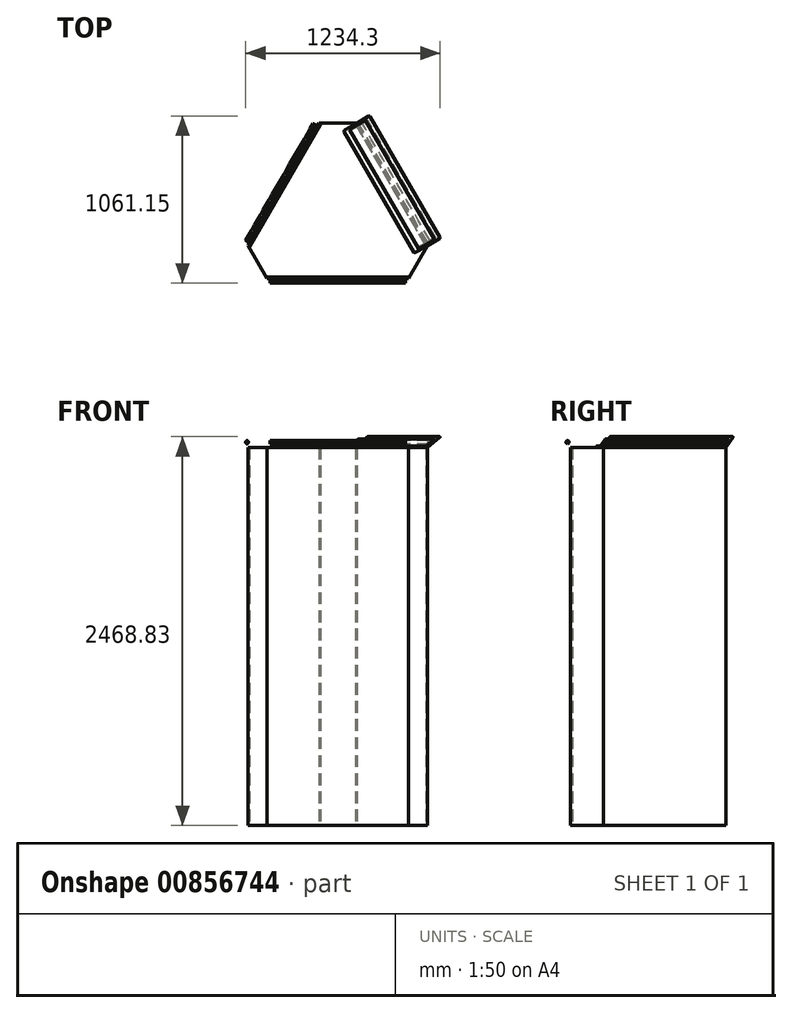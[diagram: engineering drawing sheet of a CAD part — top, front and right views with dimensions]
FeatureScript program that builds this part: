
annotation { "Feature Type Name" : "Feature", "Feature Type Description" : "" }
export const myFeature = defineFeature(function(context is Context, id is Id, definition is map)
    precondition{}
    {
        {
            var Q0;
            Q0=qCreatedBy(makeId("Top.planeOp"),FACE);
            var sketch = newSketch(context, id + "F0", { "sketchPlane" : qUnion([Q0])});
            skLineSegment(sketch, "E0", {"start": v(-570, 207.85) * mm, "end": v(-120, 987.27) * mm});
            skLineSegment(sketch, "E1", {"start": v(120, 987.27) * mm, "end": v(570, 207.85) * mm});
            skLineSegment(sketch, "E2", {"start": v(-450, 0) * mm, "end": v(450, 0) * mm});
            skLineSegment(sketch, "E3", {"start": v(-690, 0) * mm, "end": v(345, 597.56) * mm, "construction": true});
            skLineSegment(sketch, "E4", {"start": v(690, 0) * mm, "end": v(-345, 597.56) * mm, "construction": true});
            skLineSegment(sketch, "E5", {"start": v(0, 1195.12) * mm, "end": v(0, 0) * mm, "construction": true});
            skLineSegment(sketch, "E6", {"start": v(-120, 987.27) * mm, "end": v(120, 987.27) * mm});
            skLineSegment(sketch, "E7", {"start": v(-450, 0) * mm, "end": v(-570, 207.85) * mm});
            skLineSegment(sketch, "E8", {"start": v(450, 0) * mm, "end": v(570, 207.85) * mm});
            skSolve(sketch);
        }
        {
            var Q0;
            Q0=qSketchRegion(id+"F0",true);
            extrude(context, id + "F1", {"entities" : qUnion([Q0]), "depth" : 2400 * mm, "offsetDistance" : 25 * mm});
        }
        {
            var Q0;
            Q0=makeQuery(id+"F1.opExtrude","CAP_FACE",FACE,{"disambiguationData":[OSD([sQuery(id+"F0.wireOp",EDGE,"E0"),sQuery(id+"F0.wireOp",EDGE,"E1"),sQuery(id+"F0.wireOp",EDGE,"E2"),sQuery(id+"F0.wireOp",EDGE,"E6"),sQuery(id+"F0.wireOp",EDGE,"E7"),sQuery(id+"F0.wireOp",EDGE,"E8")])],"isStart":false});
            var sketch = newSketch(context, id + "F2", { "sketchPlane" : qUnion([Q0])});
            skLineSegment(sketch, "E9.0", {"start": v(-350, 40) * mm, "end": v(350, 40) * mm});
            skLineSegment(sketch, "E10.0", {"start": v(-485.36, 274.45) * mm, "end": v(-135.36, 880.67) * mm});
            skLineSegment(sketch, "E11", {"start": v(-350, 40) * mm, "end": v(-350, 90) * mm});
            skLineSegment(sketch, "E12", {"start": v(-350, 90) * mm, "end": v(350, 90) * mm});
            skLineSegment(sketch, "E13", {"start": v(350, 90) * mm, "end": v(350, 40) * mm});
            skLineSegment(sketch, "E14", {"start": v(-135.36, 880.67) * mm, "end": v(-92.06, 855.67) * mm});
            skLineSegment(sketch, "E15", {"start": v(-92.06, 855.67) * mm, "end": v(-442.06, 249.45) * mm});
            skLineSegment(sketch, "E16", {"start": v(-442.06, 249.45) * mm, "end": v(-485.36, 274.45) * mm});
            skLineSegment(sketch, "E17", {"start": v(-345, 597.56) * mm, "end": v(-140.02, 479.21) * mm, "construction": true});
            skLineSegment(sketch, "E18", {"start": v(0, 0) * mm, "end": v(0, 987.27) * mm, "construction": true});
            skLineSegment(sketch, "E19.MirrorCS", {"start": v(-92.06, 855.67) * mm, "end": v(-135.36, 880.67) * mm});
            skLineSegment(sketch, "E20.MirrorCS", {"start": v(-485.36, 274.45) * mm, "end": v(-442.06, 249.45) * mm});
            skLineSegment(sketch, "E21.MirrorCS", {"start": v(-135.36, 880.67) * mm, "end": v(-485.36, 274.45) * mm});
            skLineSegment(sketch, "E22.MirrorCS", {"start": v(-442.06, 249.45) * mm, "end": v(-92.06, 855.67) * mm});
            skLineSegment(sketch, "E23.MirrorCS", {"start": v(135.36, 880.67) * mm, "end": v(92.06, 855.67) * mm});
            skLineSegment(sketch, "E24.MirrorCS", {"start": v(442.06, 249.45) * mm, "end": v(485.36, 274.45) * mm});
            skLineSegment(sketch, "E25.MirrorCS", {"start": v(485.36, 274.45) * mm, "end": v(442.06, 249.45) * mm});
            skLineSegment(sketch, "E26.MirrorCS", {"start": v(92.06, 855.67) * mm, "end": v(135.36, 880.67) * mm});
            skLineSegment(sketch, "E27.MirrorCS", {"start": v(92.06, 855.67) * mm, "end": v(442.06, 249.45) * mm});
            skLineSegment(sketch, "E28.MirrorCS", {"start": v(485.36, 274.45) * mm, "end": v(135.36, 880.67) * mm});
            skLineSegment(sketch, "E29.MirrorCS", {"start": v(135.36, 880.67) * mm, "end": v(485.36, 274.45) * mm});
            skLineSegment(sketch, "E30.MirrorCS", {"start": v(442.06, 249.45) * mm, "end": v(92.06, 855.67) * mm});
            skSolve(sketch);
        }
        {
            var Q0;
            Q0=qCreatedBy(makeId("Right.planeOp"),FACE);
            var sketch = newSketch(context, id + "F3", { "sketchPlane" : qUnion([Q0])});
            skPoint(sketch, "E31.2", {"position": v(103.92, 2400) * mm});
            skLineSegment(sketch, "E32", {"start": v(398.37, 2400) * mm, "end": v(398.37, -119.7) * mm, "construction": true});
            skPoint(sketch, "E32.endSnap0", {"position": v(398.37, 2400) * mm});
            skSolve(sketch);
        }
        {
            var Q0;
            Q0=makeQuery(id+"F1.opExtrude","CAP_FACE",FACE,{"disambiguationData":[OSD([sQuery(id+"F0.wireOp",EDGE,"E0"),sQuery(id+"F0.wireOp",EDGE,"E1"),sQuery(id+"F0.wireOp",EDGE,"E2"),sQuery(id+"F0.wireOp",EDGE,"E6"),sQuery(id+"F0.wireOp",EDGE,"E7"),sQuery(id+"F0.wireOp",EDGE,"E8")])],"isStart":true});
            var sketch = newSketch(context, id + "F4", { "sketchPlane" : qUnion([Q0])});
            skLineSegment(sketch, "E33.0", {"start": v(-570, -207.85) * mm, "end": v(-120, -987.27) * mm});
            skLineSegment(sketch, "E33.1", {"start": v(120, -987.27) * mm, "end": v(570, -207.85) * mm});
            skLineSegment(sketch, "E33.2", {"start": v(-450, 0) * mm, "end": v(450, 0) * mm});
            skLineSegment(sketch, "E34.0", {"start": v(-561.34, -202.85) * mm, "end": v(-111.34, -982.27) * mm});
            skLineSegment(sketch, "E35.0", {"start": v(-450, -10) * mm, "end": v(450, -10) * mm});
            skLineSegment(sketch, "E36.0", {"start": v(111.34, -982.27) * mm, "end": v(561.34, -202.85) * mm});
            skLineSegment(sketch, "E37", {"start": v(-111.34, -982.27) * mm, "end": v(-120, -987.27) * mm});
            skLineSegment(sketch, "E38", {"start": v(-570, -207.85) * mm, "end": v(-561.34, -202.85) * mm});
            skLineSegment(sketch, "E39", {"start": v(-450, 0) * mm, "end": v(-450, -10) * mm});
            skLineSegment(sketch, "E40", {"start": v(450, 0) * mm, "end": v(450, -10) * mm});
            skLineSegment(sketch, "E41", {"start": v(570, -207.85) * mm, "end": v(561.34, -202.85) * mm});
            skLineSegment(sketch, "E42", {"start": v(120, -987.27) * mm, "end": v(111.34, -982.27) * mm});
            skSolve(sketch);
        }
        {
            var Q0;
            Q0=qSketchRegion(id+"F4",true);
            var Q1;
            Q1=makeQuery(id+"F1.opExtrude","CAP_FACE",FACE,{"disambiguationData":[OSD([sQuery(id+"F0.wireOp",EDGE,"E0"),sQuery(id+"F0.wireOp",EDGE,"E1"),sQuery(id+"F0.wireOp",EDGE,"E2"),sQuery(id+"F0.wireOp",EDGE,"E6"),sQuery(id+"F0.wireOp",EDGE,"E7"),sQuery(id+"F0.wireOp",EDGE,"E8")])],"isStart":false});
            extrude(context, id + "F5", {"entities" : qUnion([Q0]), "operationType" : NewBodyOperationType.REMOVE, "endBound" : BoundingType.UP_TO_SURFACE, "oppositeDirection" : true, "depth" : 25 * mm, "endBoundEntityFace" : qUnion([Q1]), "offsetDistance" : 25 * mm});
        }
        {
            var Q0;
            Q0=makeQuery(id+"F1.opExtrude","CAP_FACE",FACE,{"disambiguationData":[OSD([sQuery(id+"F0.wireOp",EDGE,"E0"),sQuery(id+"F0.wireOp",EDGE,"E1"),sQuery(id+"F0.wireOp",EDGE,"E2"),sQuery(id+"F0.wireOp",EDGE,"E6"),sQuery(id+"F0.wireOp",EDGE,"E7"),sQuery(id+"F0.wireOp",EDGE,"E8")])],"isStart":true});
            var sketch = newSketch(context, id + "F6", { "sketchPlane" : qUnion([Q0])});
            skLineSegment(sketch, "E43.0", {"start": v(-560.84, -203.71) * mm, "end": v(-111.84, -981.4) * mm});
            skLineSegment(sketch, "E44.0", {"start": v(-569.5, -208.71) * mm, "end": v(-120.5, -986.4) * mm});
            skLineSegment(sketch, "E45.0", {"start": v(-111.84, -981.4) * mm, "end": v(-120.5, -986.4) * mm});
            skLineSegment(sketch, "E46.0", {"start": v(-569.5, -208.71) * mm, "end": v(-560.84, -203.71) * mm});
            skPoint(sketch, "E47.orphan", {"position": v(-561.34, -202.85) * mm});
            skPoint(sketch, "E48.orphan", {"position": v(-111.34, -982.27) * mm});
            skSolve(sketch);
        }
        {
            var Q0;
            Q0=qSketchRegion(id+"F6",true);
            var Q1;
            Q1=makeQuery(id+"F1.opExtrude","CAP_FACE",FACE,{"disambiguationData":[OSD([sQuery(id+"F0.wireOp",EDGE,"E0"),sQuery(id+"F0.wireOp",EDGE,"E1"),sQuery(id+"F0.wireOp",EDGE,"E2"),sQuery(id+"F0.wireOp",EDGE,"E6"),sQuery(id+"F0.wireOp",EDGE,"E7"),sQuery(id+"F0.wireOp",EDGE,"E8")])],"isStart":false});
            extrude(context, id + "F7", {"entities" : qUnion([Q0]), "endBound" : BoundingType.UP_TO_SURFACE, "oppositeDirection" : true, "depth" : 25 * mm, "endBoundEntityFace" : qUnion([Q1]), "offsetDistance" : 25 * mm});
        }
        {
            var Q0;
            Q0=makeQuery(id+"F7.opExtrude","SWEPT_BODY",BODY,{"disambiguationData":[OSD([sQuery(id+"F6.wireOp",EDGE,"E43.0"),sQuery(id+"F6.wireOp",EDGE,"E44.0"),sQuery(id+"F6.wireOp",EDGE,"E45.0"),sQuery(id+"F6.wireOp",EDGE,"E46.0")])]});
            var Q1;
            Q1=sQuery(id+"F3.wireOp",EDGE,"E32");
            circularPattern(context, id + "F8", {"entities" : qUnion([Q0]), "axis" : qUnion([Q1]), "angle" : 360 * degree, "instanceCount" : 3, "equalSpace" : true});
        }
        {
            var Q0;
            Q0=makeQuery(id+"F1.opExtrude","SWEPT_FACE",FACE,{"disambiguationData":[OSD([sQuery(id+"F0.wireOp",EDGE,"E7")])]});
            var Q1;
            Q1=makeQuery(id+"F7.opExtrude","SWEPT_EDGE",EDGE,{"disambiguationData":[OSD([sQuery(id+"F6.wireOp",EDGE,"E44.0"),sQuery(id+"F6.wireOp",EDGE,"E46.0")])]});
            cPlane(context, id + "F9", {"entities" : qUnion([Q0, Q1]), "cplaneType" : CPlaneType.LINE_ANGLE, "offset" : 25 * mm, "angle" : 90 * degree, "width" : 150 * mm, "height" : 150 * mm});
        }
        {
            var Q0;
            Q0=qCreatedBy(id+"F9.planeOp",FACE);
            cPlane(context, id + "F10", {"entities" : qUnion([Q0]), "cplaneType" : CPlaneType.OFFSET, "offset" : 120.5 * mm, "width" : 150 * mm, "height" : 150 * mm});
        }
        {
            var Q0;
            Q0=qCreatedBy(id+"F10.planeOp",FACE);
            var sketch = newSketch(context, id + "F11", { "sketchPlane" : qUnion([Q0])});
            skPoint(sketch, "E49.0", {"position": v(597.56, 2400) * mm});
            skLineSegment(sketch, "E50", {"start": v(597.56, 2400) * mm, "end": v(695.86, 2468.83) * mm});
            skLineSegment(sketch, "E51", {"start": v(695.86, 2468.83) * mm, "end": v(675.86, 2468.83) * mm});
            skLineSegment(sketch, "E52", {"start": v(675.86, 2468.83) * mm, "end": v(591.84, 2410) * mm});
            skLineSegment(sketch, "E53", {"start": v(577.56, 2400) * mm, "end": v(597.56, 2400) * mm});
            skLineSegment(sketch, "E54", {"start": v(577.56, 2400) * mm, "end": v(527.56, 2400) * mm});
            skLineSegment(sketch, "E55", {"start": v(527.56, 2400) * mm, "end": v(527.56, 2410) * mm});
            skLineSegment(sketch, "E56", {"start": v(527.56, 2410) * mm, "end": v(591.84, 2410) * mm});
            skSolve(sketch);
        }
        {
            var Q0;
            Q0 = qSketchRegion(id + "F11", true);
            var Q1;
            Q1=makeQuery(id+"F8.opPattern","COPY",EDGE,{"derivedFrom":makeQuery(id+"F7.opExtrude","CAP_EDGE",EDGE,{"disambiguationData":[OSD([sQuery(id+"F6.wireOp",EDGE,"E44.0")])],"isStart":false}),"instanceName":"1"});
            sweep(context, id + "F12", {"profiles" : qUnion([Q0]), "path" : qUnion([Q1])});
        }
        {
            var Q0;
            Q0=makeQuery(id+"F12.opSweep","SWEPT_FACE",FACE,{"disambiguationData":[OSD([sQuery(id+"F0.wireOp",EDGE,"E0"),sQuery(id+"F0.wireOp",EDGE,"E1"),sQuery(id+"F0.wireOp",EDGE,"E2"),sQuery(id+"F0.wireOp",EDGE,"E6"),sQuery(id+"F0.wireOp",EDGE,"E7"),sQuery(id+"F0.wireOp",EDGE,"E8"),sQuery(id+"F6.wireOp",EDGE,"E44.0"),sQuery(id+"F11.wireOp",EDGE,"E55")])]});
            var sketch = newSketch(context, id + "F13", { "sketchPlane" : qUnion([Q0])});
            skLineSegment(sketch, "E57.bottom", {"start": v(-774, 2410) * mm, "end": v(84, 2410) * mm});
            skLineSegment(sketch, "E57.top", {"start": v(-774, 2448.83) * mm, "end": v(84, 2448.83) * mm});
            skLineSegment(sketch, "E57.left", {"start": v(-774, 2410) * mm, "end": v(-774, 2448.83) * mm});
            skLineSegment(sketch, "E57.right", {"start": v(84, 2410) * mm, "end": v(84, 2448.83) * mm});
            skSolve(sketch);
        }
        {
            var Q0;
            Q0 = qSketchRegion(id + "F13", true);
            extrude(context, id + "F14", {"entities" : qUnion([Q0]), "operationType" : NewBodyOperationType.REMOVE, "oppositeDirection" : true, "depth" : 301 * mm, "offsetDistance" : 25 * mm});
        }
        {
            var Q0;
            Q0=makeQuery(id+"F12.opSweep","CAP_FACE",FACE,{"disambiguationData":[OSD([sQuery(id+"F0.wireOp",EDGE,"E0"),sQuery(id+"F0.wireOp",EDGE,"E1"),sQuery(id+"F0.wireOp",EDGE,"E2"),sQuery(id+"F0.wireOp",EDGE,"E6"),sQuery(id+"F0.wireOp",EDGE,"E7"),sQuery(id+"F0.wireOp",EDGE,"E8"),sQuery(id+"F6.wireOp",EDGE,"E44.0"),sQuery(id+"F6.wireOp",EDGE,"E46.0"),sQuery(id+"F11.wireOp",EDGE,"E50"),sQuery(id+"F11.wireOp",EDGE,"E51"),sQuery(id+"F11.wireOp",EDGE,"E52"),sQuery(id+"F11.wireOp",EDGE,"E53"),sQuery(id+"F11.wireOp",EDGE,"E54"),sQuery(id+"F11.wireOp",EDGE,"E55"),sQuery(id+"F11.wireOp",EDGE,"E56")])],"isStart":true});
            var sketch = newSketch(context, id + "F15", { "sketchPlane" : qUnion([Q0])});
            skLineSegment(sketch, "E58.0", {"start": v(-546.84, 2410) * mm, "end": v(-538.12, 2410) * mm});
            skLineSegment(sketch, "E58.1", {"start": v(-654.43, 2453.83) * mm, "end": v(-647.3, 2448.83) * mm});
            skPoint(sketch, "E59.0", {"position": v(-657.3, 2448.83) * mm});
            skLineSegment(sketch, "E60", {"start": v(-647.3, 2448.83) * mm, "end": v(-602.3, 2448.83) * mm});
            skLineSegment(sketch, "E61", {"start": v(-602.3, 2448.83) * mm, "end": v(-546.84, 2410) * mm});
            skLineSegment(sketch, "E62.0", {"start": v(-600.72, 2453.83) * mm, "end": v(-538.12, 2410) * mm});
            skLineSegment(sketch, "E62.1", {"start": v(-654.43, 2453.83) * mm, "end": v(-600.72, 2453.83) * mm});
            skPoint(sketch, "E63.orphan", {"position": v(-675.86, 2468.83) * mm});
            skPoint(sketch, "E64.orphan", {"position": v(-591.84, 2410) * mm});
            skPoint(sketch, "E65.orphan", {"position": v(-527.56, 2410) * mm});
            skSolve(sketch);
        }
        {
            var Q0;
            Q0 = qSketchRegion(id + "F15", true);
            var Q1;
            Q1=makeQuery(id+"F14.boolean.opBoolean","COPY",FACE,{"derivedFrom":makeQuery(id+"F14.opExtrude","SWEPT_FACE",FACE,{"disambiguationData":[OSD([sQuery(id+"F13.wireOp",EDGE,"E57.right")])]})});
            extrude(context, id + "F16", {"entities" : qUnion([Q0]), "operationType" : NewBodyOperationType.ADD, "endBound" : BoundingType.UP_TO_SURFACE, "oppositeDirection" : true, "depth" : 25 * mm, "endBoundEntityFace" : qUnion([Q1]), "hasOffset" : true, "offsetDistance" : 10 * mm, "offsetOppositeDirection" : true});
        }
        {
            var Q0;
            Q0=makeQuery(id+"F16.opExtrude","CAP_FACE",FACE,{"disambiguationData":[OSD([sQuery(id+"F15.wireOp",EDGE,"E58.0"),sQuery(id+"F15.wireOp",EDGE,"E58.1"),sQuery(id+"F15.wireOp",EDGE,"E60"),sQuery(id+"F15.wireOp",EDGE,"E61"),sQuery(id+"F15.wireOp",EDGE,"E62.0"),sQuery(id+"F15.wireOp",EDGE,"E62.1")])],"isStart":false});
            var sketch = newSketch(context, id + "F17", { "sketchPlane" : qUnion([Q0])});
            skLineSegment(sketch, "E66.0", {"start": v(600.72, 2453.83) * mm, "end": v(538.12, 2410) * mm});
            skLineSegment(sketch, "E66.1", {"start": v(654.43, 2453.83) * mm, "end": v(600.72, 2453.83) * mm});
            skPoint(sketch, "E66.2", {"position": v(569.42, 2431.91) * mm});
            skLineSegment(sketch, "E67.0", {"start": v(654.43, 2453.83) * mm, "end": v(591.84, 2410) * mm});
            skLineSegment(sketch, "E67.1", {"start": v(591.84, 2410) * mm, "end": v(538.12, 2410) * mm});
            skPoint(sketch, "E68.orphan", {"position": v(527.56, 2410) * mm});
            skPoint(sketch, "E69.orphan", {"position": v(675.86, 2468.83) * mm});
            skSolve(sketch);
        }
        {
            var Q0;
            Q0 = qSketchRegion(id + "F17", true);
            var Q1;
            Q1 = qConstructionFilter(qBodyType(qCreatedBy(id + "F17" ,EDGE), BodyType.WIRE), ConstructionObject.NO);
            extrude(context, id + "F18", {"entities" : qUnion([Q0]), "operationType" : NewBodyOperationType.ADD, "surfaceOperationType" : NewSurfaceOperationType.ADD, "surfaceEntities" : qUnion([Q1]), "oppositeDirection" : true, "depth" : 10 * mm, "offsetDistance" : 25 * mm});
        }
        {
            var Q0;
            Q0=makeQuery(id+"F12.opSweep","SWEPT_FACE",FACE,{"disambiguationData":[OSD([sQuery(id+"F0.wireOp",EDGE,"E0"),sQuery(id+"F0.wireOp",EDGE,"E1"),sQuery(id+"F0.wireOp",EDGE,"E2"),sQuery(id+"F0.wireOp",EDGE,"E6"),sQuery(id+"F0.wireOp",EDGE,"E7"),sQuery(id+"F0.wireOp",EDGE,"E8"),sQuery(id+"F6.wireOp",EDGE,"E44.0"),sQuery(id+"F11.wireOp",EDGE,"E55")])]});
            var sketch = newSketch(context, id + "F19", { "sketchPlane" : qUnion([Q0])});
            skLineSegment(sketch, "E70.bottom", {"start": v(-794, 2410) * mm, "end": v(-784, 2410) * mm});
            skLineSegment(sketch, "E70.top", {"start": v(-794, 2453.83) * mm, "end": v(-784, 2453.83) * mm});
            skLineSegment(sketch, "E70.left", {"start": v(-794, 2410) * mm, "end": v(-794, 2453.83) * mm});
            skLineSegment(sketch, "E70.right", {"start": v(-784, 2410) * mm, "end": v(-784, 2453.83) * mm});
            skSolve(sketch);
        }
        {
            var Q0;
            Q0 = qSketchRegion(id + "F19", true);
            var Q1;
            {var subQ1=sQuery(id+"F6.wireOp",EDGE,"E44.0");var subQ2=sQuery(id+"F11.wireOp",EDGE,"E52");Q1=makeQuery(id+"F16.boolean.opBoolean","SPLIT",FACE,{"disambiguationData":[TD([makeQuery(id+"F14.boolean.opBoolean","COPY",FACE,{"derivedFrom":makeQuery(id+"F14.opExtrude","SWEPT_FACE",FACE,{"disambiguationData":[OSD([sQuery(id+"F13.wireOp",EDGE,"E57.left")])]})})])],"derivedFrom":makeQuery(id+"F12.opSweep","SWEPT_FACE",FACE,{"disambiguationData":[OSD([subQ1,subQ2])]})});}
            extrude(context, id + "F20", {"entities" : qUnion([Q0]), "operationType" : NewBodyOperationType.REMOVE, "endBound" : BoundingType.UP_TO_SURFACE, "oppositeDirection" : true, "depth" : 25 * mm, "endBoundEntityFace" : qUnion([Q1]), "offsetDistance" : 25 * mm});
        }
        {
            var Q0;
            Q0=makeQuery(id+"F20.boolean.opBoolean","COPY",FACE,{"derivedFrom":makeQuery(id+"F20.opExtrude","SWEPT_FACE",FACE,{"disambiguationData":[OSD([sQuery(id+"F19.wireOp",EDGE,"E70.right")])]})});
            var sketch = newSketch(context, id + "F21", { "sketchPlane" : qUnion([Q0])});
            skLineSegment(sketch, "E71.0", {"start": v(-654.43, 2453.83) * mm, "end": v(-600.72, 2453.83) * mm});
            skLineSegment(sketch, "E71.1", {"start": v(-600.72, 2453.83) * mm, "end": v(-538.12, 2410) * mm});
            skLineSegment(sketch, "E72.0", {"start": v(-654.43, 2453.83) * mm, "end": v(-591.84, 2410) * mm});
            skLineSegment(sketch, "E72.1", {"start": v(-591.84, 2410) * mm, "end": v(-538.12, 2410) * mm});
            skPoint(sketch, "E73.orphan", {"position": v(-675.86, 2468.83) * mm});
            skPoint(sketch, "E74.orphan", {"position": v(-527.56, 2410) * mm});
            skSolve(sketch);
        }
        {
            var Q0;
            Q0 = qSketchRegion(id + "F21", true);
            extrude(context, id + "F22", {"entities" : qUnion([Q0]), "operationType" : NewBodyOperationType.ADD, "oppositeDirection" : true, "depth" : 10 * mm, "offsetDistance" : 25 * mm});
        }
        {
            var Q0;
            Q0=makeQuery(id+"F12.opSweep","SWEPT_FACE",FACE,{"disambiguationData":[OSD([sQuery(id+"F0.wireOp",EDGE,"E0"),sQuery(id+"F0.wireOp",EDGE,"E1"),sQuery(id+"F0.wireOp",EDGE,"E2"),sQuery(id+"F0.wireOp",EDGE,"E6"),sQuery(id+"F0.wireOp",EDGE,"E7"),sQuery(id+"F0.wireOp",EDGE,"E8"),sQuery(id+"F6.wireOp",EDGE,"E44.0"),sQuery(id+"F11.wireOp",EDGE,"E55")])]});
            extrude(context, id + "F23", {"entities" : qUnion([Q0]), "operationType" : NewBodyOperationType.ADD, "depth" : 25 * mm, "offsetDistance" : 25 * mm});
        }
        {
            var Q0;
            Q0=makeQuery(id+"F18.boolean.opBoolean","MERGE",FACE,{"derivedFrom":[makeQuery(id+"F14.boolean.opBoolean","COPY",FACE,{"derivedFrom":makeQuery(id+"F14.opExtrude","SWEPT_FACE",FACE,{"disambiguationData":[OSD([sQuery(id+"F13.wireOp",EDGE,"E57.right")])]})}),makeQuery(id+"F18.opExtrude","CAP_FACE",FACE,{"disambiguationData":[OSD([sQuery(id+"F17.wireOp",EDGE,"E66.0"),sQuery(id+"F17.wireOp",EDGE,"E66.1"),sQuery(id+"F17.wireOp",EDGE,"E67.0"),sQuery(id+"F17.wireOp",EDGE,"E67.1")])],"isStart":false})]});
            var sketch = newSketch(context, id + "F24", { "sketchPlane" : qUnion([Q0])});
            skLineSegment(sketch, "E75.0", {"start": v(-611.84, 2410) * mm, "end": v(-546.84, 2410) * mm});
            skLineSegment(sketch, "E75.1", {"start": v(-597.56, 2400) * mm, "end": v(-611.84, 2410) * mm});
            skLineSegment(sketch, "E76.0", {"start": v(-532.56, 2400) * mm, "end": v(-597.56, 2400) * mm});
            skLineSegment(sketch, "E77", {"start": v(-546.84, 2410) * mm, "end": v(-532.56, 2400) * mm});
            skPoint(sketch, "E78.orphan", {"position": v(-695.86, 2468.83) * mm});
            skPoint(sketch, "E79.orphan", {"position": v(-502.56, 2400) * mm});
            skSolve(sketch);
        }
        {
            var Q0;
            Q0 = qSketchRegion(id + "F24", true);
            var Q1;
            Q1=makeQuery(id+"F22.boolean.opBoolean","MERGE",FACE,{"derivedFrom":[makeQuery(id+"F14.boolean.opBoolean","COPY",FACE,{"derivedFrom":makeQuery(id+"F14.opExtrude","SWEPT_FACE",FACE,{"disambiguationData":[OSD([sQuery(id+"F13.wireOp",EDGE,"E57.left")])]})}),makeQuery(id+"F22.opExtrude","CAP_FACE",FACE,{"disambiguationData":[OSD([sQuery(id+"F21.wireOp",EDGE,"E71.0"),sQuery(id+"F21.wireOp",EDGE,"E71.1"),sQuery(id+"F21.wireOp",EDGE,"E72.0"),sQuery(id+"F21.wireOp",EDGE,"E72.1")])],"isStart":false})]});
            extrude(context, id + "F25", {"entities" : qUnion([Q0]), "operationType" : NewBodyOperationType.REMOVE, "endBound" : BoundingType.UP_TO_SURFACE, "depth" : 25 * mm, "endBoundEntityFace" : qUnion([Q1]), "offsetDistance" : 25 * mm});
        }
        {
            var Q0;
            Q0=makeQuery(id+"F25.boolean.opBoolean","MERGE",FACE,{"derivedFrom":[makeQuery(id+"F22.boolean.opBoolean","MERGE",FACE,{"derivedFrom":[makeQuery(id+"F14.boolean.opBoolean","COPY",FACE,{"derivedFrom":makeQuery(id+"F14.opExtrude","SWEPT_FACE",FACE,{"disambiguationData":[OSD([sQuery(id+"F13.wireOp",EDGE,"E57.left")])]})}),makeQuery(id+"F22.opExtrude","CAP_FACE",FACE,{"disambiguationData":[OSD([sQuery(id+"F21.wireOp",EDGE,"E71.0"),sQuery(id+"F21.wireOp",EDGE,"E71.1"),sQuery(id+"F21.wireOp",EDGE,"E72.0"),sQuery(id+"F21.wireOp",EDGE,"E72.1")])],"isStart":false})]})],"fromTools":[makeQuery(id+"F25.opExtrude","CAP_FACE",FACE,{"disambiguationData":[OSD([sQuery(id+"F24.wireOp",EDGE,"E75.0"),sQuery(id+"F24.wireOp",EDGE,"E75.1"),sQuery(id+"F24.wireOp",EDGE,"E76.0"),sQuery(id+"F24.wireOp",EDGE,"E77")])],"isStart":false})]});
            var sketch = newSketch(context, id + "F26", { "sketchPlane" : qUnion([Q0])});
            skLineSegment(sketch, "E80.0", {"start": v(667.3, 2448.83) * mm, "end": v(602.3, 2448.83) * mm, "construction": true});
            skLineSegment(sketch, "E80.1", {"start": v(532.56, 2400) * mm, "end": v(602.3, 2448.83) * mm, "construction": true});
            skLineSegment(sketch, "E80.2", {"start": v(667.3, 2448.83) * mm, "end": v(597.56, 2400) * mm, "construction": true});
            skPoint(sketch, "E80.3", {"position": v(632.43, 2424.41) * mm});
            skCircle(sketch, "E81", {"center": v(617.43, 2433.83) * mm, "radius": 10 * mm});
            skSolve(sketch);
        }
        {
            var Q0;
            Q0 = qSketchRegion(id + "F26", true);
            var Q1;
            Q1=makeQuery(id+"F25.boolean.opBoolean","MERGE",FACE,{"derivedFrom":[makeQuery(id+"F18.boolean.opBoolean","MERGE",FACE,{"derivedFrom":[makeQuery(id+"F14.boolean.opBoolean","COPY",FACE,{"derivedFrom":makeQuery(id+"F14.opExtrude","SWEPT_FACE",FACE,{"disambiguationData":[OSD([sQuery(id+"F13.wireOp",EDGE,"E57.right")])]})}),makeQuery(id+"F18.opExtrude","CAP_FACE",FACE,{"disambiguationData":[OSD([sQuery(id+"F17.wireOp",EDGE,"E66.0"),sQuery(id+"F17.wireOp",EDGE,"E66.1"),sQuery(id+"F17.wireOp",EDGE,"E67.0"),sQuery(id+"F17.wireOp",EDGE,"E67.1")])],"isStart":false})]})],"fromTools":[makeQuery(id+"F25.opExtrude","CAP_FACE",FACE,{"disambiguationData":[OSD([sQuery(id+"F24.wireOp",EDGE,"E75.0"),sQuery(id+"F24.wireOp",EDGE,"E75.1"),sQuery(id+"F24.wireOp",EDGE,"E76.0"),sQuery(id+"F24.wireOp",EDGE,"E77")])],"isStart":true})]});
            extrude(context, id + "F27", {"entities" : qUnion([Q0]), "endBound" : BoundingType.UP_TO_SURFACE, "depth" : 25 * mm, "endBoundEntityFace" : qUnion([Q1]), "offsetDistance" : 25 * mm});
        }
        {
            var Q0;
            Q0=makeQuery(id+"F16.opExtrude","SWEPT_EDGE",EDGE,{"disambiguationData":[OSD([sQuery(id+"F15.wireOp",EDGE,"E62.0"),sQuery(id+"F15.wireOp",EDGE,"E62.1")])]});
            var Q1;
            {var subQ0=sQuery(id+"F11.wireOp",EDGE,"E56");var subQ1=sQuery(id+"F6.wireOp",EDGE,"E44.0");var subQ2=sQuery(id+"F0.wireOp",EDGE,"E8");var subQ3=sQuery(id+"F0.wireOp",EDGE,"E7");var subQ4=sQuery(id+"F0.wireOp",EDGE,"E6");var subQ5=sQuery(id+"F0.wireOp",EDGE,"E2");var subQ6=sQuery(id+"F0.wireOp",EDGE,"E1");var subQ7=sQuery(id+"F0.wireOp",EDGE,"E0");var subQ8=sQuery(id+"F11.wireOp",EDGE,"E52");Q1=makeQuery(id+"F14.boolean.opBoolean","SPLIT",EDGE,{"disambiguationData":[TD([makeQuery(id+"F14.opExtrude","SWEPT_FACE",FACE,{"disambiguationData":[OSD([sQuery(id+"F13.wireOp",EDGE,"E57.left")])]})])],"derivedFrom":makeQuery(id+"F12.opSweep","SWEPT_EDGE",EDGE,{"disambiguationData":[OSD([subQ7,subQ6,subQ5,subQ4,subQ3,subQ2,subQ1,subQ8,subQ0])]})});}
            var Q2;
            {var subQ0=sQuery(id+"F11.wireOp",EDGE,"E56");var subQ1=sQuery(id+"F6.wireOp",EDGE,"E44.0");var subQ2=sQuery(id+"F0.wireOp",EDGE,"E8");var subQ3=sQuery(id+"F0.wireOp",EDGE,"E7");var subQ4=sQuery(id+"F0.wireOp",EDGE,"E6");var subQ5=sQuery(id+"F0.wireOp",EDGE,"E2");var subQ6=sQuery(id+"F0.wireOp",EDGE,"E1");var subQ7=sQuery(id+"F0.wireOp",EDGE,"E0");var subQ8=sQuery(id+"F11.wireOp",EDGE,"E52");Q2=makeQuery(id+"F14.boolean.opBoolean","SPLIT",EDGE,{"disambiguationData":[TD([makeQuery(id+"F14.opExtrude","SWEPT_FACE",FACE,{"disambiguationData":[OSD([sQuery(id+"F13.wireOp",EDGE,"E57.right")])]})])],"derivedFrom":makeQuery(id+"F12.opSweep","SWEPT_EDGE",EDGE,{"disambiguationData":[OSD([subQ7,subQ6,subQ5,subQ4,subQ3,subQ2,subQ1,subQ8,subQ0])]})});}
            fillet(context, id + "F28", {"entities" : qUnion([Q0, Q1, Q2]), "radius" : 10 * mm, "tangentPropagation" : true, "allowEdgeOverflow" : false});
        }
        {
            var Q0;
            Q0=makeQuery(id+"F12.opSweep","CAP_EDGE",EDGE,{"disambiguationData":[OSD([sQuery(id+"F0.wireOp",EDGE,"E0"),sQuery(id+"F0.wireOp",EDGE,"E1"),sQuery(id+"F0.wireOp",EDGE,"E2"),sQuery(id+"F0.wireOp",EDGE,"E6"),sQuery(id+"F0.wireOp",EDGE,"E7"),sQuery(id+"F0.wireOp",EDGE,"E8"),sQuery(id+"F6.wireOp",EDGE,"E44.0"),sQuery(id+"F6.wireOp",EDGE,"E46.0"),sQuery(id+"F11.wireOp",EDGE,"E51")])],"isStart":true});
            var Q1;
            Q1=makeQuery(id+"F12.opSweep","CAP_EDGE",EDGE,{"disambiguationData":[OSD([sQuery(id+"F0.wireOp",EDGE,"E0"),sQuery(id+"F0.wireOp",EDGE,"E1"),sQuery(id+"F0.wireOp",EDGE,"E2"),sQuery(id+"F0.wireOp",EDGE,"E6"),sQuery(id+"F0.wireOp",EDGE,"E7"),sQuery(id+"F0.wireOp",EDGE,"E8"),sQuery(id+"F6.wireOp",EDGE,"E44.0"),sQuery(id+"F6.wireOp",EDGE,"E45.0"),sQuery(id+"F11.wireOp",EDGE,"E51")])],"isStart":false});
            var Q2;
            Q2=makeQuery(id+"F23.opExtrude","CAP_EDGE",EDGE,{"disambiguationData":[OSD([sQuery(id+"F0.wireOp",EDGE,"E0"),sQuery(id+"F0.wireOp",EDGE,"E1"),sQuery(id+"F0.wireOp",EDGE,"E2"),sQuery(id+"F0.wireOp",EDGE,"E6"),sQuery(id+"F0.wireOp",EDGE,"E7"),sQuery(id+"F0.wireOp",EDGE,"E8"),sQuery(id+"F6.wireOp",EDGE,"E44.0"),sQuery(id+"F6.wireOp",EDGE,"E46.0"),sQuery(id+"F11.wireOp",EDGE,"E55")])],"isStart":false});
            var Q3;
            Q3=makeQuery(id+"F23.opExtrude","CAP_EDGE",EDGE,{"disambiguationData":[OSD([sQuery(id+"F0.wireOp",EDGE,"E0"),sQuery(id+"F0.wireOp",EDGE,"E1"),sQuery(id+"F0.wireOp",EDGE,"E2"),sQuery(id+"F0.wireOp",EDGE,"E6"),sQuery(id+"F0.wireOp",EDGE,"E7"),sQuery(id+"F0.wireOp",EDGE,"E8"),sQuery(id+"F6.wireOp",EDGE,"E44.0"),sQuery(id+"F6.wireOp",EDGE,"E45.0"),sQuery(id+"F11.wireOp",EDGE,"E55")])],"isStart":false});
            var Q4;
            Q4=makeQuery(id+"F16.opExtrude","SWEPT_EDGE",EDGE,{"disambiguationData":[OSD([sQuery(id+"F15.wireOp",EDGE,"E60"),sQuery(id+"F15.wireOp",EDGE,"E61")])]});
            fillet(context, id + "F29", {"entities" : qUnion([Q0, Q1, Q2, Q3, Q4]), "radius" : 5 * mm, "tangentPropagation" : true, "allowEdgeOverflow" : false});
        }
        {
            var Q0;
            Q0=makeQuery(id+"F16.opExtrude","CAP_EDGE",EDGE,{"disambiguationData":[OSD([sQuery(id+"F15.wireOp",EDGE,"E62.1")])],"isStart":false});
            var Q1;
            Q1=makeQuery(id+"F20.boolean.opBoolean","INTERSECT",EDGE,{"derivedFrom":[makeQuery(id+"F16.opExtrude","SWEPT_FACE",FACE,{"disambiguationData":[OSD([sQuery(id+"F15.wireOp",EDGE,"E62.0")])]}),makeQuery(id+"F20.opExtrude","SWEPT_FACE",FACE,{"disambiguationData":[OSD([sQuery(id+"F19.wireOp",EDGE,"E70.right")])]})]});
            var Q2;
            Q2=makeQuery(id+"F12.opSweep","SWEPT_EDGE",EDGE,{"disambiguationData":[OSD([sQuery(id+"F0.wireOp",EDGE,"E0"),sQuery(id+"F0.wireOp",EDGE,"E1"),sQuery(id+"F0.wireOp",EDGE,"E2"),sQuery(id+"F0.wireOp",EDGE,"E6"),sQuery(id+"F0.wireOp",EDGE,"E7"),sQuery(id+"F0.wireOp",EDGE,"E8"),sQuery(id+"F6.wireOp",EDGE,"E44.0"),sQuery(id+"F11.wireOp",EDGE,"E51"),sQuery(id+"F11.wireOp",EDGE,"E52")])]});
            var Q3;
            Q3=makeQuery(id+"F12.opSweep","CAP_EDGE",EDGE,{"disambiguationData":[OSD([sQuery(id+"F0.wireOp",EDGE,"E0"),sQuery(id+"F0.wireOp",EDGE,"E1"),sQuery(id+"F0.wireOp",EDGE,"E2"),sQuery(id+"F0.wireOp",EDGE,"E6"),sQuery(id+"F0.wireOp",EDGE,"E7"),sQuery(id+"F0.wireOp",EDGE,"E8"),sQuery(id+"F6.wireOp",EDGE,"E44.0"),sQuery(id+"F6.wireOp",EDGE,"E46.0"),sQuery(id+"F11.wireOp",EDGE,"E50")])],"isStart":true});
            fillet(context, id + "F30", {"entities" : qUnion([Q0, Q1, Q2, Q3]), "radius" : 2 * mm, "tangentPropagation" : true, "allowEdgeOverflow" : false});
        }
        {
            var Q0;
            Q0=makeQuery(id+"F22.boolean.opBoolean","INTERSECT",EDGE,{"derivedFrom":[makeQuery(id+"F16.boolean.opBoolean","MERGE",FACE,{"derivedFrom":[makeQuery(id+"F14.boolean.opBoolean","COPY",FACE,{"derivedFrom":makeQuery(id+"F14.opExtrude","SWEPT_FACE",FACE,{"disambiguationData":[OSD([sQuery(id+"F13.wireOp",EDGE,"E57.top")])]})}),makeQuery(id+"F16.opExtrude","SWEPT_FACE",FACE,{"disambiguationData":[OSD([sQuery(id+"F15.wireOp",EDGE,"E60")])]})]}),makeQuery(id+"F22.opExtrude","CAP_FACE",FACE,{"disambiguationData":[OSD([sQuery(id+"F21.wireOp",EDGE,"E71.0"),sQuery(id+"F21.wireOp",EDGE,"E71.1"),sQuery(id+"F21.wireOp",EDGE,"E72.0"),sQuery(id+"F21.wireOp",EDGE,"E72.1")])],"isStart":false})]});
            var Q1;
            Q1=makeQuery(id+"F25.boolean.opBoolean","MERGE",EDGE,{"derivedFrom":[makeQuery(id+"F18.boolean.opBoolean","INTERSECT",EDGE,{"derivedFrom":[makeQuery(id+"F16.opExtrude","SWEPT_FACE",FACE,{"disambiguationData":[OSD([sQuery(id+"F15.wireOp",EDGE,"E61")])]}),makeQuery(id+"F18.opExtrude","CAP_FACE",FACE,{"disambiguationData":[OSD([sQuery(id+"F17.wireOp",EDGE,"E66.0"),sQuery(id+"F17.wireOp",EDGE,"E66.1"),sQuery(id+"F17.wireOp",EDGE,"E67.0"),sQuery(id+"F17.wireOp",EDGE,"E67.1")])],"isStart":false})]})],"fromTools":[makeQuery(id+"F25.opExtrude","CAP_EDGE",EDGE,{"disambiguationData":[OSD([sQuery(id+"F24.wireOp",EDGE,"E77")])],"isStart":true})]});
            fillet(context, id + "F31", {"entities" : qUnion([Q0, Q1]), "radius" : 2 * mm, "tangentPropagation" : true, "allowEdgeOverflow" : false});
        }
        {
            var Q0;
            Q0=makeQuery(id+"F12.opSweep","SWEPT_BODY",BODY,{"disambiguationData":[OSD([sQuery(id+"F0.wireOp",EDGE,"E0"),sQuery(id+"F0.wireOp",EDGE,"E1"),sQuery(id+"F0.wireOp",EDGE,"E2"),sQuery(id+"F0.wireOp",EDGE,"E6"),sQuery(id+"F0.wireOp",EDGE,"E7"),sQuery(id+"F0.wireOp",EDGE,"E8"),sQuery(id+"F6.wireOp",EDGE,"E44.0"),sQuery(id+"F11.wireOp",EDGE,"E50"),sQuery(id+"F11.wireOp",EDGE,"E51"),sQuery(id+"F11.wireOp",EDGE,"E52"),sQuery(id+"F11.wireOp",EDGE,"E53"),sQuery(id+"F11.wireOp",EDGE,"E54"),sQuery(id+"F11.wireOp",EDGE,"E55"),sQuery(id+"F11.wireOp",EDGE,"E56")])]});
            var Q1;
            Q1=makeQuery(id+"F27.opExtrude","SWEPT_BODY",BODY,{"disambiguationData":[OSD([sQuery(id+"F26.wireOp",EDGE,"E81")])]});
            var Q2;
            Q2=sQuery(id+"F3.wireOp",EDGE,"E32");
            circularPattern(context, id + "F32", {"entities" : qUnion([Q0, Q1]), "axis" : qUnion([Q2]), "angle" : 360 * degree, "instanceCount" : 3, "equalSpace" : true});
        }
    });
